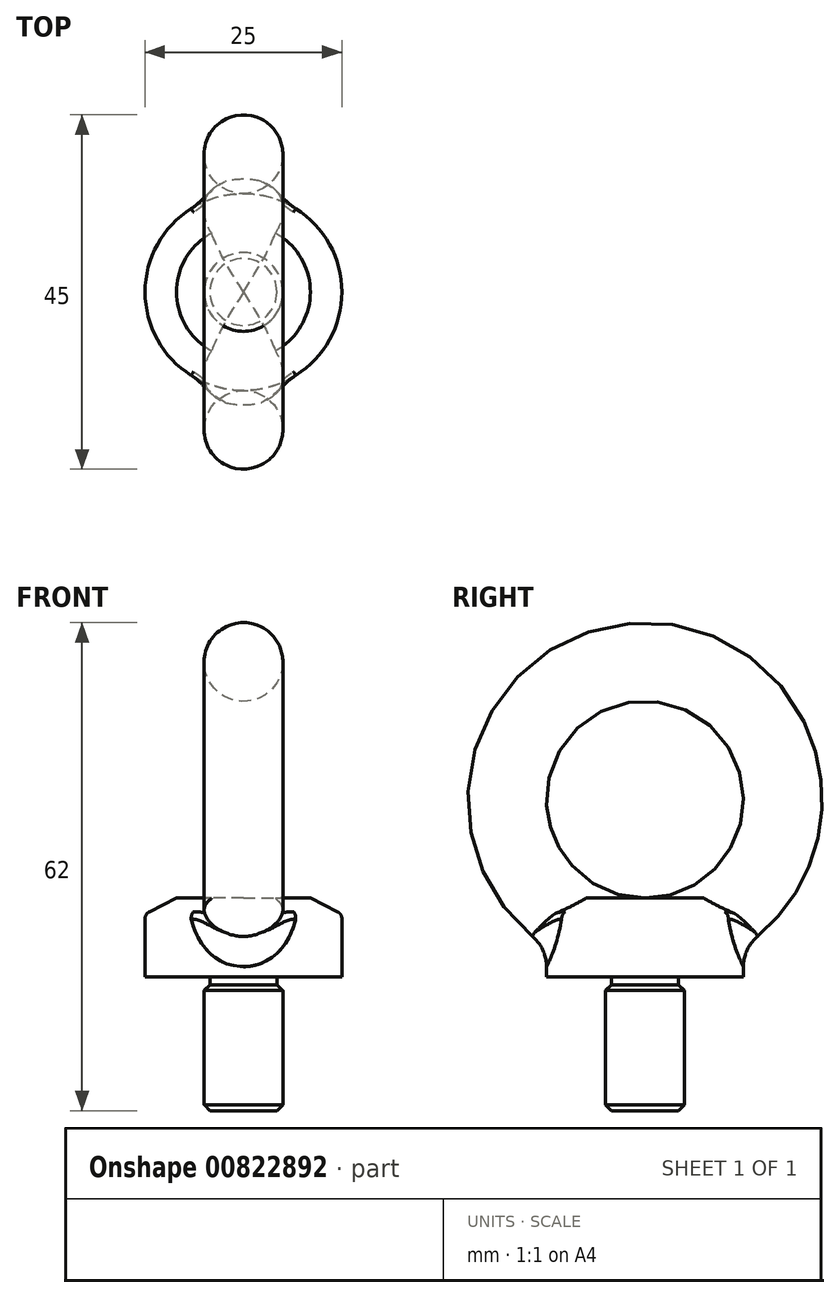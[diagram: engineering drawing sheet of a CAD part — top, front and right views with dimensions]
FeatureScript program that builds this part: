
annotation { "Feature Type Name" : "Feature", "Feature Type Description" : "" }
export const myFeature = defineFeature(function(context is Context, id is Id, definition is map)
    precondition{}
    {
        {
            var Q0;
            Q0=qCreatedBy(makeId("Front.planeOp"),FACE);
            var sketch = newSketch(context, id + "F0", { "sketchPlane" : qUnion([Q0])});
            skLineSegment(sketch, "E0", {"start": v(0, 0) * mm, "end": v(-8.5, 0) * mm});
            skLineSegment(sketch, "E1", {"start": v(-12.5, -2) * mm, "end": v(-12.5, -10) * mm});
            skLineSegment(sketch, "E2", {"start": v(-12.5, -10) * mm, "end": v(-4.25, -10) * mm});
            skLineSegment(sketch, "E3", {"start": v(-4.25, -10) * mm, "end": v(-4.25, -11) * mm});
            skLineSegment(sketch, "E4", {"start": v(-4.25, -11) * mm, "end": v(-5, -11) * mm});
            skLineSegment(sketch, "E5", {"start": v(-5, -11) * mm, "end": v(-5, -27) * mm});
            skLineSegment(sketch, "E6", {"start": v(-5, -27) * mm, "end": v(0, -27) * mm});
            skLineSegment(sketch, "E7", {"start": v(0, -27) * mm, "end": v(0, 0) * mm});
            skLineSegment(sketch, "E8", {"start": v(0, -27) * mm, "end": v(0, -60.93) * mm, "construction": true});
            skLineSegment(sketch, "E9", {"start": v(-12.5, -2) * mm, "end": v(-8.5, 0) * mm});
            skSolve(sketch);
        }
        {
            var Q0;
            Q0 = qSketchRegion(id + "F0", true);
            var Q1;
            Q1=sQuery(id+"F0.wireOp",EDGE,"E8");
            revolve(context, id + "F1", {"surfaceOperationType" : NewSurfaceOperationType.NEW, "entities" : qUnion([Q0]), "axis" : qUnion([Q1]), "revolveType" : RevolveType.FULL});
        }
        {
            var Q0;
            Q0=qCreatedBy(makeId("Front.planeOp"),FACE);
            var sketch = newSketch(context, id + "F2", { "sketchPlane" : qUnion([Q0])});
            skCircle(sketch, "E10", {"center": v(0, 30) * mm, "radius": 5 * mm});
            skPoint(sketch, "E11", {"position": v(0, 25) * mm});
            skLineSegment(sketch, "E12", {"start": v(0, 25) * mm, "end": v(0, 0) * mm, "construction": true});
            skLineSegment(sketch, "E13", {"start": v(0, 12.5) * mm, "end": v(16.16, 12.5) * mm, "construction": true});
            skSolve(sketch);
        }
        {
            var Q0;
            Q0 = qSketchRegion(id + "F2", true);
            var Q1;
            Q1=sQuery(id+"F2.wireOp",EDGE,"E13");
            revolve(context, id + "F3", {"operationType" : NewBodyOperationType.ADD, "surfaceOperationType" : NewSurfaceOperationType.NEW, "entities" : qUnion([Q0]), "axis" : qUnion([Q1]), "revolveType" : RevolveType.FULL});
        }
        {
            var Q0;
            Q0=makeQuery(id+"F3.boolean.opBoolean","INTERSECT",EDGE,{"disambiguationData":[OD(0.0)],"derivedFrom":[makeQuery(id+"F1.opRevolve","SWEPT_FACE",FACE,{"disambiguationData":[OSD([sQuery(id+"F0.wireOp",EDGE,"E1")])]}),makeQuery(id+"F3.opRevolve","SWEPT_FACE",FACE,{"disambiguationData":[OSD([sQuery(id+"F2.wireOp",EDGE,"E10")])]})]});
            var Q1;
            Q1=makeQuery(id+"F3.boolean.opBoolean","INTERSECT",EDGE,{"disambiguationData":[OD(1.0)],"derivedFrom":[makeQuery(id+"F1.opRevolve","SWEPT_FACE",FACE,{"disambiguationData":[OSD([sQuery(id+"F0.wireOp",EDGE,"E1")])]}),makeQuery(id+"F3.opRevolve","SWEPT_FACE",FACE,{"disambiguationData":[OSD([sQuery(id+"F2.wireOp",EDGE,"E10")])]})]});
            fillet(context, id + "F4", {"entities" : qUnion([Q0, Q1]), "radius" : 5 * mm, "allowEdgeOverflow" : false});
        }
        {
            var Q0;
            Q0=makeQuery(id+"F3.boolean.opBoolean","SPLIT",EDGE,{"disambiguationData":[OD(1.0)],"derivedFrom":makeQuery(id+"F1.opRevolve","SWEPT_EDGE",EDGE,{"disambiguationData":[OSD([sQuery(id+"F0.wireOp",EDGE,"E1"),sQuery(id+"F0.wireOp",EDGE,"E9")])]})});
            var Q1;
            Q1=makeQuery(id+"F3.boolean.opBoolean","SPLIT",EDGE,{"disambiguationData":[OD(0.0)],"derivedFrom":makeQuery(id+"F1.opRevolve","SWEPT_EDGE",EDGE,{"disambiguationData":[OSD([sQuery(id+"F0.wireOp",EDGE,"E1"),sQuery(id+"F0.wireOp",EDGE,"E9")])]})});
            fillet(context, id + "F5", {"entities" : qUnion([Q0, Q1]), "radius" : 1 * mm, "tangentPropagation" : true, "allowEdgeOverflow" : false});
        }
        {
            var Q0;
            Q0=makeQuery(id+"F1.opRevolve","SWEPT_FACE",FACE,{"disambiguationData":[OSD([sQuery(id+"F0.wireOp",EDGE,"E5")])]});
            chamfer(context, id + "F6", {"entities" : qUnion([Q0]), "width" : 0.75 * mm, "tangentPropagation" : true});
        }
    });
